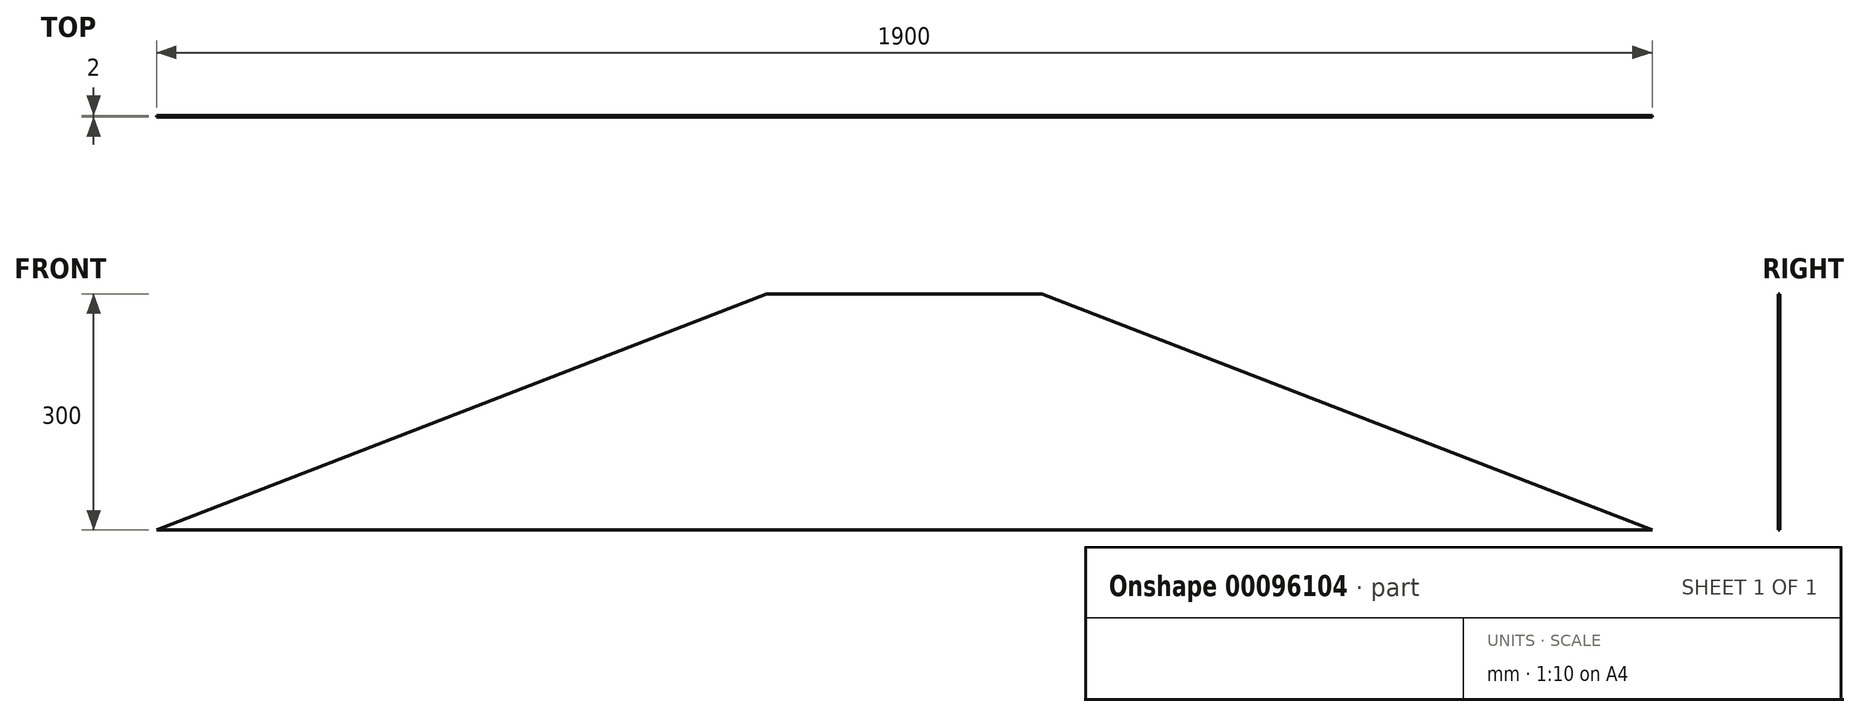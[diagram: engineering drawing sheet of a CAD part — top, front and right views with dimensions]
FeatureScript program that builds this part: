
annotation { "Feature Type Name" : "Feature", "Feature Type Description" : "" }
export const myFeature = defineFeature(function(context is Context, id is Id, definition is map)
    precondition{}
    {
        {
            var Q0;
            Q0=qCreatedBy(makeId("Front.planeOp"),FACE);
            var sketch = newSketch(context, id + "F0", { "sketchPlane" : qUnion([Q0])});
            skLineSegment(sketch, "E0", {"start": v(0, 0) * mm, "end": v(-950, 0) * mm});
            skLineSegment(sketch, "E1", {"start": v(0, 0) * mm, "end": v(950, 0) * mm});
            skLineSegment(sketch, "E2", {"start": v(0, 300) * mm, "end": v(-175, 300) * mm});
            skLineSegment(sketch, "E3", {"start": v(0, 300) * mm, "end": v(175, 300) * mm});
            skLineSegment(sketch, "E4", {"start": v(-950, 0) * mm, "end": v(-175, 300) * mm});
            skLineSegment(sketch, "E5", {"start": v(175, 300) * mm, "end": v(950, 0) * mm});
            skSolve(sketch);
        }
        {
            var Q0;
            Q0 = qSketchRegion(id + "F0", true);
            extrude(context, id + "F1", {"entities" : qUnion([Q0]), "depth" : 2 * mm});
        }
    });
